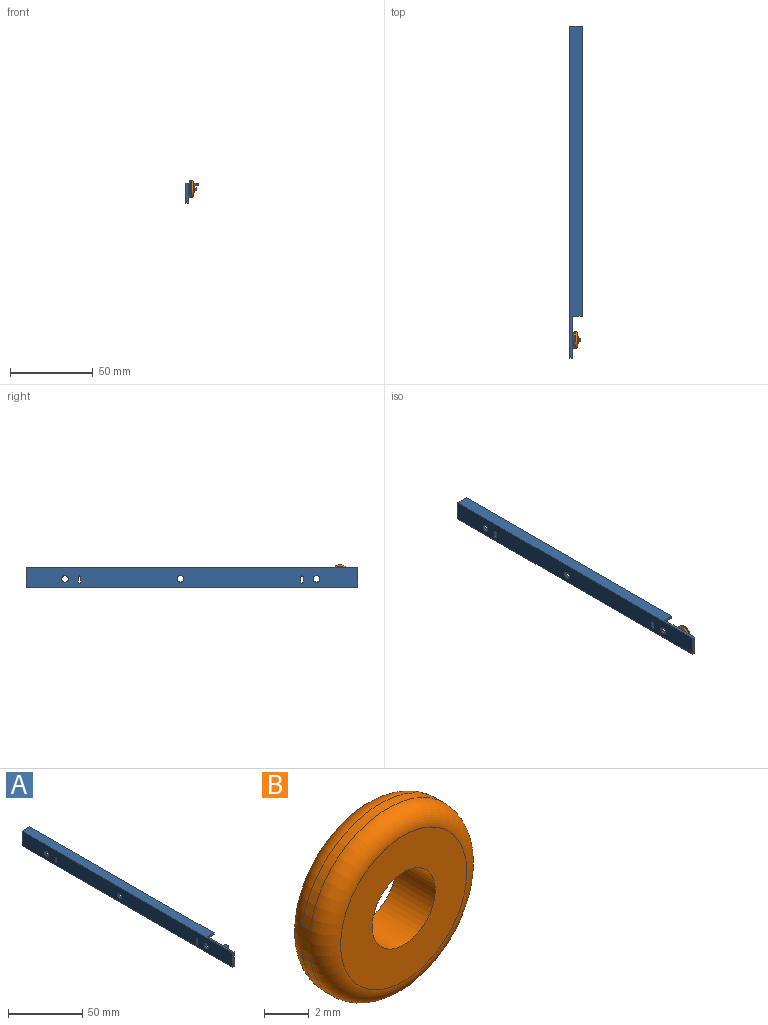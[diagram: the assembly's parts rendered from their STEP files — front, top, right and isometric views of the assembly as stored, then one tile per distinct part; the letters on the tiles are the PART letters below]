
ASSEMBLY  parts=2 mates=1
PART A: 24 faces, bbox 7.5x200x12 mm
  f0: plane 200x12mm, normal (-1,0,0), area 2349.8mm2, adj f3,f4,f5,f7,f9,f10,f11,f12
  f1: plane 200x12mm, normal (1,0,0), area 2074.7mm2, adj f3,f4,f5,f6,f7,f8,f9,f10
  f2: plane 175x1.5mm, normal (1,0,0), area 262.5mm2, adj f3,f6,f7,f8
  f3: plane 200x7.5mm, normal (0,0,1), area 1350mm2, adj f0,f1,f2,f4,f7,f8
  f4: plane 12x1.5mm, normal (0,-1,0), area 18mm2, adj f0,f1,f3,f5
  f5: plane 200x1.5mm, normal (0,0,-1), area 300mm2, adj f0,f1,f4,f7
  f6: plane 175x6mm, normal (0,0,-1), area 1050mm2, adj f1,f2,f7,f8
  f7: plane 12x7.5mm, normal (0,1,0), area 27mm2, adj f0,f1,f2,f3,f5,f6
  f8: plane 6x1.5mm, normal (0,-1,0), area 9mm2, adj f1,f2,f3,f6
  f9: cylinder r=2mm len=4mm, axis (1,0,0), area 18.8mm2, adj f0,f1
  f10: cylinder r=2mm len=4mm, axis (1,0,0), area 18.8mm2, adj f0,f1
  f11: cylinder r=0.75mm len=1.5mm, axis (1,0,0), area 3.5mm2, adj f0,f1,f12,f14
  f12: plane 3x1.5mm, normal (0,1,0), area 4.5mm2, adj f0,f1,f11,f13
  f13: cylinder r=0.75mm len=1.5mm, axis (1,0,0), area 3.5mm2, adj f0,f1,f12,f14
  f14: plane 3x1.5mm, normal (0,-1,0), area 4.5mm2, adj f0,f1,f11,f13
  f15: cylinder r=0.75mm len=1.5mm, axis (1,0,0), area 3.5mm2, adj f0,f1,f16,f18
  f16: plane 3x1.5mm, normal (0,1,0), area 4.5mm2, adj f0,f1,f15,f17
  f17: cylinder r=0.75mm len=1.5mm, axis (1,0,0), area 3.5mm2, adj f0,f1,f16,f18
  f18: plane 3x1.5mm, normal (0,-1,0), area 4.5mm2, adj f0,f1,f15,f17
  f19: cylinder r=2mm len=4mm, axis (1,0,0), area 18.8mm2, adj f0,f1
  f20: cylinder r=2mm len=4mm, axis (-1,0,0), area 44mm2, adj f1,f21
  f21: plane 4x4mm, normal (1,0,0), area 10.8mm2, adj f20,f23
  f22: plane 1.5x1.5mm, normal (1,0,0), area 1.8mm2, adj f23
  f23: cylinder r=0.75mm len=1.5mm, axis (-1,0,0), area 7.1mm2, adj f21,f22
PART B: 6 faces, bbox 10.8x2.5x10.8 mm
  f0: cylinder r=5mm len=10mm, axis (0,1,0), area 15.7mm2, adj f3,f4
  f1: plane 8x8mm, normal (0,-1,0), area 37.7mm2, adj f3,f5
  f2: plane 8x8mm, normal (0,1,0), area 37.7mm2, adj f4,f5
  f3: torus R=4mm, axis (0,-1,0), area 45.8mm2, adj f0,f1
  f4: torus R=4mm, axis (0,-1,0), area 45.8mm2, adj f0,f2
  f5: cylinder r=2mm len=4mm, axis (0,-1,0), area 31.4mm2, adj f1,f2
PLACE A t=(25.95,-6.88,-20.59)mm
PLACE B rot(axis=(-0.58,-0.58,-0.58),120deg) t=(30.45,3.88,-12.09)mm
MATE revolute B.f5 <-> A.f20  axis (-1,0,0) through (29.2,3.88,-12.09)mm
